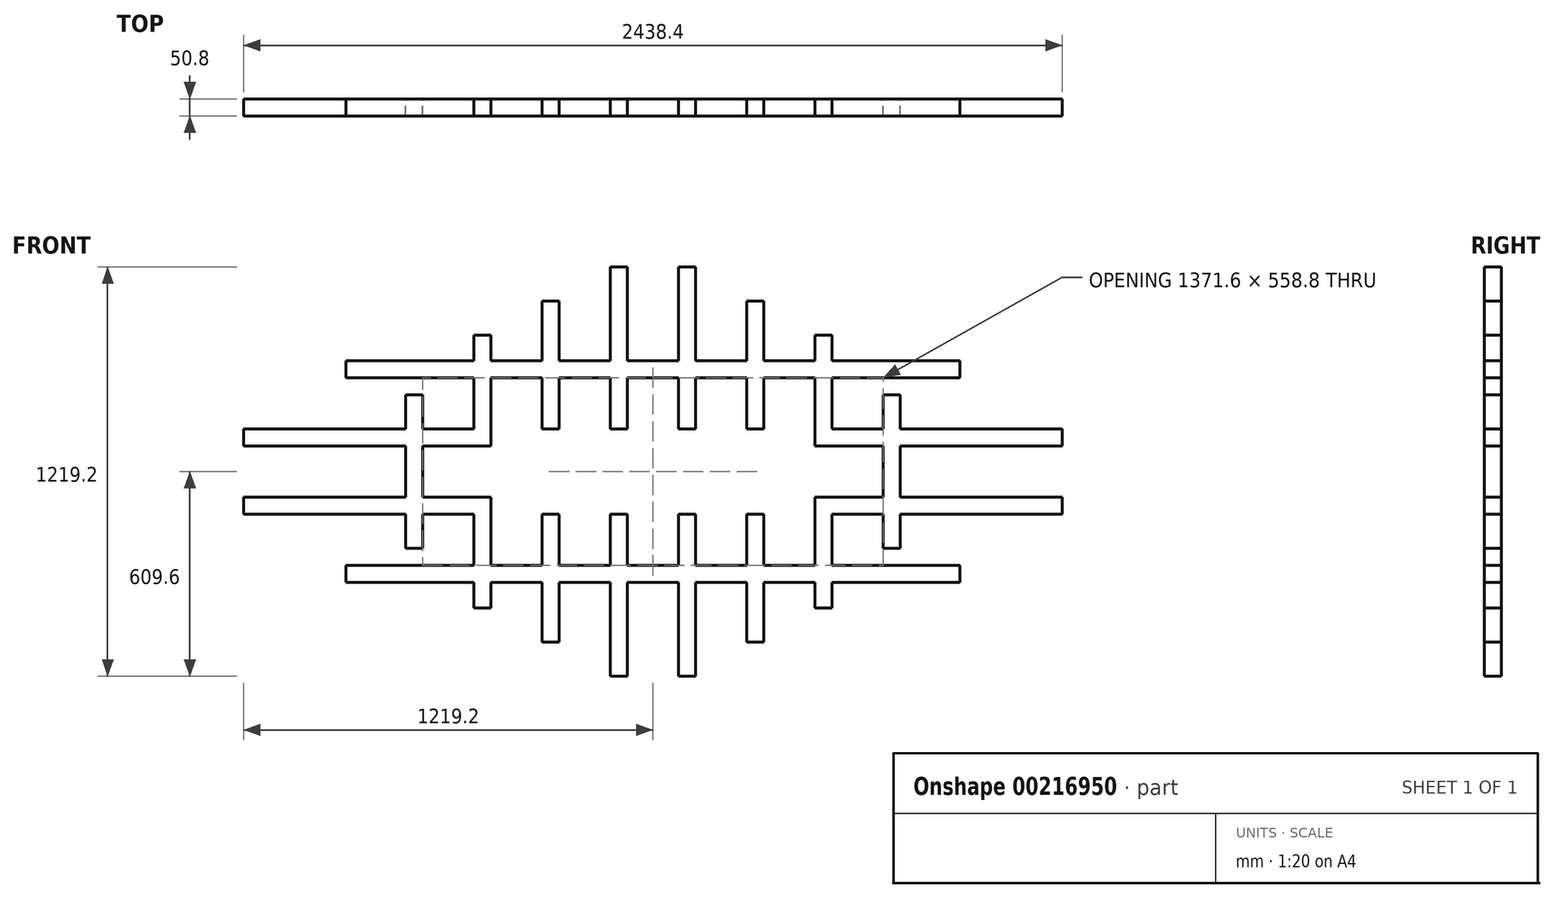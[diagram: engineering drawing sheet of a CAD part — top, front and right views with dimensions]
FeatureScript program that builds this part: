
annotation { "Feature Type Name" : "Feature", "Feature Type Description" : "" }
export const myFeature = defineFeature(function(context is Context, id is Id, definition is map)
    precondition{}
    {
        {
            var Q0;
            Q0=qCreatedBy(makeId("Front.planeOp"),FACE);
            var sketch = newSketch(context, id + "F0", { "sketchPlane" : qUnion([Q0])});
            skLineSegment(sketch, "E0.bottom", {"start": v(-1219.2, 76.2) * mm, "end": v(1219.2, 76.2) * mm});
            skLineSegment(sketch, "E0.top", {"start": v(-1219.2, -76.2) * mm, "end": v(1219.2, -76.2) * mm});
            skPoint(sketch, "E0.middle", {"position": v(0, 0) * mm});
            skLineSegment(sketch, "E1.top", {"start": v(-1219.2, 127) * mm, "end": v(1219.2, 127) * mm});
            skLineSegment(sketch, "E1.left", {"start": v(-1219.2, 76.2) * mm, "end": v(-1219.2, 127) * mm});
            skLineSegment(sketch, "E1.right", {"start": v(1219.2, 76.2) * mm, "end": v(1219.2, 127) * mm});
            skLineSegment(sketch, "E2.top", {"start": v(-1219.2, -127) * mm, "end": v(1219.2, -127) * mm});
            skLineSegment(sketch, "E2.left", {"start": v(-1219.2, -76.2) * mm, "end": v(-1219.2, -127) * mm});
            skLineSegment(sketch, "E2.right", {"start": v(1219.2, -76.2) * mm, "end": v(1219.2, -127) * mm});
            skLineSegment(sketch, "E3", {"start": v(0, -776.46) * mm, "end": v(0, 885.21) * mm, "construction": true});
            skPoint(sketch, "E3.startSnap0", {"position": v(0, -127) * mm});
            skLineSegment(sketch, "E4", {"start": v(-1506.22, 0) * mm, "end": v(1703.54, 0) * mm, "construction": true});
            skLineSegment(sketch, "E5", {"start": v(0, 127) * mm, "end": v(0, 304.8) * mm});
            skLineSegment(sketch, "E6", {"start": v(0, -127) * mm, "end": v(0, -304.8) * mm});
            skLineSegment(sketch, "E7.bottom", {"start": v(-914.4, -279.4) * mm, "end": v(914.4, -279.4) * mm});
            skLineSegment(sketch, "E7.top", {"start": v(-914.4, -330.2) * mm, "end": v(914.4, -330.2) * mm});
            skLineSegment(sketch, "E7.left", {"start": v(-914.4, -279.4) * mm, "end": v(-914.4, -330.2) * mm});
            skLineSegment(sketch, "E7.right", {"start": v(914.4, -279.4) * mm, "end": v(914.4, -330.2) * mm});
            skPoint(sketch, "E7.middle", {"position": v(0, -304.8) * mm});
            skLineSegment(sketch, "E8.bottom", {"start": v(-914.4, 330.2) * mm, "end": v(914.4, 330.2) * mm});
            skLineSegment(sketch, "E8.top", {"start": v(-914.4, 279.4) * mm, "end": v(914.4, 279.4) * mm});
            skLineSegment(sketch, "E8.left", {"start": v(-914.4, 330.2) * mm, "end": v(-914.4, 279.4) * mm});
            skLineSegment(sketch, "E8.right", {"start": v(914.4, 330.2) * mm, "end": v(914.4, 279.4) * mm});
            skPoint(sketch, "E8.middle", {"position": v(0, 304.8) * mm});
            skLineSegment(sketch, "E9", {"start": v(0, 0) * mm, "end": v(101.6, 0) * mm});
            skLineSegment(sketch, "E10", {"start": v(101.6, 0) * mm, "end": v(-101.6, 0) * mm});
            skLineSegment(sketch, "E11", {"start": v(101.6, 0) * mm, "end": v(304.8, 0) * mm});
            skLineSegment(sketch, "E12", {"start": v(304.8, 0) * mm, "end": v(508, 0) * mm});
            skLineSegment(sketch, "E13", {"start": v(508, 0) * mm, "end": v(711.2, 0) * mm});
            skLineSegment(sketch, "E14", {"start": v(-101.6, 0) * mm, "end": v(-304.8, 0) * mm});
            skLineSegment(sketch, "E15", {"start": v(-304.8, 0) * mm, "end": v(-508, 0) * mm});
            skLineSegment(sketch, "E16", {"start": v(-508, 0) * mm, "end": v(-711.2, 0) * mm});
            skLineSegment(sketch, "E17.bottom", {"start": v(127, 609.6) * mm, "end": v(76.2, 609.6) * mm});
            skLineSegment(sketch, "E17.top", {"start": v(127, -609.6) * mm, "end": v(76.2, -609.6) * mm});
            skLineSegment(sketch, "E17.left", {"start": v(127, 609.6) * mm, "end": v(127, -609.6) * mm});
            skLineSegment(sketch, "E17.right", {"start": v(76.2, 609.6) * mm, "end": v(76.2, -609.6) * mm});
            skPoint(sketch, "E17.middle", {"position": v(101.6, 0) * mm});
            skLineSegment(sketch, "E18.bottom", {"start": v(-76.2, 609.6) * mm, "end": v(-127, 609.6) * mm});
            skLineSegment(sketch, "E18.top", {"start": v(-76.2, -609.6) * mm, "end": v(-127, -609.6) * mm});
            skLineSegment(sketch, "E18.left", {"start": v(-76.2, 609.6) * mm, "end": v(-76.2, -609.6) * mm});
            skLineSegment(sketch, "E18.right", {"start": v(-127, 609.6) * mm, "end": v(-127, -609.6) * mm});
            skPoint(sketch, "E18.middle", {"position": v(-101.6, 0) * mm});
            skLineSegment(sketch, "E19.bottom", {"start": v(-278.94, 508) * mm, "end": v(-330.66, 508) * mm});
            skLineSegment(sketch, "E19.top", {"start": v(-278.94, -508) * mm, "end": v(-330.66, -508) * mm});
            skLineSegment(sketch, "E19.left", {"start": v(-278.94, 508) * mm, "end": v(-278.94, -508) * mm});
            skLineSegment(sketch, "E19.right", {"start": v(-330.66, 508) * mm, "end": v(-330.66, -508) * mm});
            skPoint(sketch, "E19.middle", {"position": v(-304.8, 0) * mm});
            skLineSegment(sketch, "E20.bottom", {"start": v(330.2, 508) * mm, "end": v(279.4, 508) * mm});
            skLineSegment(sketch, "E20.top", {"start": v(330.2, -508) * mm, "end": v(279.4, -508) * mm});
            skLineSegment(sketch, "E20.left", {"start": v(330.2, 508) * mm, "end": v(330.2, -508) * mm});
            skLineSegment(sketch, "E20.right", {"start": v(279.4, 508) * mm, "end": v(279.4, -508) * mm});
            skPoint(sketch, "E20.middle", {"position": v(304.8, 0) * mm});
            skLineSegment(sketch, "E21.bottom", {"start": v(-533.4, 406.4) * mm, "end": v(-482.6, 406.4) * mm});
            skLineSegment(sketch, "E21.top", {"start": v(-533.4, -406.4) * mm, "end": v(-482.6, -406.4) * mm});
            skLineSegment(sketch, "E21.left", {"start": v(-533.4, 406.4) * mm, "end": v(-533.4, -406.4) * mm});
            skLineSegment(sketch, "E21.right", {"start": v(-482.6, 406.4) * mm, "end": v(-482.6, -406.4) * mm});
            skPoint(sketch, "E21.middle", {"position": v(-508, 0) * mm});
            skLineSegment(sketch, "E22.bottom", {"start": v(533.4, 406.4) * mm, "end": v(482.6, 406.4) * mm});
            skLineSegment(sketch, "E22.top", {"start": v(533.4, -406.4) * mm, "end": v(482.6, -406.4) * mm});
            skLineSegment(sketch, "E22.left", {"start": v(533.4, 406.4) * mm, "end": v(533.4, -406.4) * mm});
            skLineSegment(sketch, "E22.right", {"start": v(482.6, 406.4) * mm, "end": v(482.6, -406.4) * mm});
            skPoint(sketch, "E22.middle", {"position": v(508, 0) * mm});
            skLineSegment(sketch, "E23.bottom", {"start": v(-685.8, 228.6) * mm, "end": v(-736.6, 228.6) * mm});
            skLineSegment(sketch, "E23.top", {"start": v(-685.8, -228.6) * mm, "end": v(-736.6, -228.6) * mm});
            skLineSegment(sketch, "E23.left", {"start": v(-685.8, 228.6) * mm, "end": v(-685.8, -228.6) * mm});
            skLineSegment(sketch, "E23.right", {"start": v(-736.6, 228.6) * mm, "end": v(-736.6, -228.6) * mm});
            skPoint(sketch, "E23.middle", {"position": v(-711.2, 0) * mm});
            skLineSegment(sketch, "E24.bottom", {"start": v(736.6, 228.6) * mm, "end": v(685.8, 228.6) * mm});
            skLineSegment(sketch, "E24.top", {"start": v(736.6, -228.6) * mm, "end": v(685.8, -228.6) * mm});
            skLineSegment(sketch, "E24.left", {"start": v(736.6, 228.6) * mm, "end": v(736.6, -228.6) * mm});
            skLineSegment(sketch, "E24.right", {"start": v(685.8, 228.6) * mm, "end": v(685.8, -228.6) * mm});
            skPoint(sketch, "E24.middle", {"position": v(711.2, 0) * mm});
            skSolve(sketch);
        }
        {
            var Q0;
            Q0 = qSketchRegion(id + "F0", true);
            var Q1;
            {var subQ0=sQuery(id+"F0.wireOp",EDGE,"E19.right");var subQ1=sQuery(id+"F0.wireOp",EDGE,"E1.top");var subQ2=makeQuery(id+"F0.imprint","INTERSECT",VERTEX,{"derivedFrom":[subQ1,subQ0]});Q1=makeQuery(id+"F0.imprint","IMPRINT",FACE,{"disambiguationData":[TD([[makeQuery(id+"F0.imprint","IMPRINT",EDGE,{"disambiguationData":[TD([[subQ2,-1.0]])],"derivedFrom":subQ1}),1.0]])]});}
            var Q2;
            {var subQ0=sQuery(id+"F0.wireOp",EDGE,"E18.right");var subQ1=sQuery(id+"F0.wireOp",EDGE,"E1.top");var subQ2=makeQuery(id+"F0.imprint","INTERSECT",VERTEX,{"derivedFrom":[subQ1,subQ0]});Q2=makeQuery(id+"F0.imprint","IMPRINT",FACE,{"disambiguationData":[TD([[makeQuery(id+"F0.imprint","IMPRINT",EDGE,{"disambiguationData":[TD([[subQ2,-1.0]])],"derivedFrom":subQ1}),1.0]])]});}
            var Q3;
            {var subQ0=sQuery(id+"F0.wireOp",EDGE,"E17.right");var subQ1=sQuery(id+"F0.wireOp",EDGE,"E1.top");var subQ2=makeQuery(id+"F0.imprint","INTERSECT",VERTEX,{"derivedFrom":[subQ1,subQ0]});Q3=makeQuery(id+"F0.imprint","IMPRINT",FACE,{"disambiguationData":[TD([[makeQuery(id+"F0.imprint","IMPRINT",EDGE,{"disambiguationData":[TD([[subQ2,-1.0]])],"derivedFrom":subQ1}),1.0]])]});}
            var Q4;
            {var subQ0=sQuery(id+"F0.wireOp",EDGE,"E20.right");var subQ1=sQuery(id+"F0.wireOp",EDGE,"E1.top");var subQ2=makeQuery(id+"F0.imprint","INTERSECT",VERTEX,{"derivedFrom":[subQ1,subQ0]});Q4=makeQuery(id+"F0.imprint","IMPRINT",FACE,{"disambiguationData":[TD([[makeQuery(id+"F0.imprint","IMPRINT",EDGE,{"disambiguationData":[TD([[subQ2,-1.0]])],"derivedFrom":subQ1}),1.0]])]});}
            var Q5;
            {var subQ1=sQuery(id+"F0.wireOp",EDGE,"E0.bottom");var subQ7=sQuery(id+"F0.wireOp",EDGE,"E20.right");var subQ8=makeQuery(id+"F0.imprint","INTERSECT",VERTEX,{"derivedFrom":[subQ1,subQ7]});Q5=makeQuery(id+"F0.imprint","IMPRINT",FACE,{"disambiguationData":[TD([[makeQuery(id+"F0.imprint","IMPRINT",EDGE,{"disambiguationData":[TD([[subQ8,-1.0]])],"derivedFrom":subQ1}),-1.0]])]});}
            var Q6;
            {var subQ1=sQuery(id+"F0.wireOp",EDGE,"E0.top");var subQ7=sQuery(id+"F0.wireOp",EDGE,"E20.right");var subQ9=makeQuery(id+"F0.imprint","INTERSECT",VERTEX,{"derivedFrom":[subQ1,subQ7]});Q6=makeQuery(id+"F0.imprint","IMPRINT",FACE,{"disambiguationData":[TD([[makeQuery(id+"F0.imprint","IMPRINT",EDGE,{"disambiguationData":[TD([[subQ9,-1.0]])],"derivedFrom":subQ1}),1.0]])]});}
            var Q7;
            {var subQ0=sQuery(id+"F0.wireOp",EDGE,"E20.right");var subQ1=sQuery(id+"F0.wireOp",EDGE,"E0.top");var subQ2=makeQuery(id+"F0.imprint","INTERSECT",VERTEX,{"derivedFrom":[subQ1,subQ0]});Q7=makeQuery(id+"F0.imprint","IMPRINT",FACE,{"disambiguationData":[TD([[makeQuery(id+"F0.imprint","IMPRINT",EDGE,{"disambiguationData":[TD([[subQ2,-1.0]])],"derivedFrom":subQ1}),-1.0]])]});}
            var Q8;
            {var subQ0=sQuery(id+"F0.wireOp",EDGE,"E20.right");var subQ1=sQuery(id+"F0.wireOp",EDGE,"E2.top");var subQ2=makeQuery(id+"F0.imprint","INTERSECT",VERTEX,{"derivedFrom":[subQ1,subQ0]});Q8=makeQuery(id+"F0.imprint","IMPRINT",FACE,{"disambiguationData":[TD([[makeQuery(id+"F0.imprint","IMPRINT",EDGE,{"disambiguationData":[TD([[subQ2,-1.0]])],"derivedFrom":subQ1}),-1.0]])]});}
            var Q9;
            {var subQ0=sQuery(id+"F0.wireOp",EDGE,"E20.right");var subQ1=sQuery(id+"F0.wireOp",EDGE,"E0.bottom");var subQ2=makeQuery(id+"F0.imprint","INTERSECT",VERTEX,{"derivedFrom":[subQ1,subQ0]});Q9=makeQuery(id+"F0.imprint","IMPRINT",FACE,{"disambiguationData":[TD([[makeQuery(id+"F0.imprint","IMPRINT",EDGE,{"disambiguationData":[TD([[subQ2,-1.0]])],"derivedFrom":subQ1}),1.0]])]});}
            var Q10;
            {var subQ5=sQuery(id+"F0.wireOp",EDGE,"E0.bottom");var subQ7=sQuery(id+"F0.wireOp",EDGE,"E22.right");var subQ9=makeQuery(id+"F0.imprint","INTERSECT",VERTEX,{"derivedFrom":[subQ5,subQ7]});Q10=makeQuery(id+"F0.imprint","IMPRINT",FACE,{"disambiguationData":[TD([[makeQuery(id+"F0.imprint","IMPRINT",EDGE,{"disambiguationData":[TD([[subQ9,-1.0]])],"derivedFrom":subQ5}),-1.0]])]});}
            var Q11;
            {var subQ5=sQuery(id+"F0.wireOp",EDGE,"E0.top");var subQ7=sQuery(id+"F0.wireOp",EDGE,"E22.right");var subQ8=makeQuery(id+"F0.imprint","INTERSECT",VERTEX,{"derivedFrom":[subQ5,subQ7]});Q11=makeQuery(id+"F0.imprint","IMPRINT",FACE,{"disambiguationData":[TD([[makeQuery(id+"F0.imprint","IMPRINT",EDGE,{"disambiguationData":[TD([[subQ8,-1.0]])],"derivedFrom":subQ5}),1.0]])]});}
            var Q12;
            {var subQ0=sQuery(id+"F0.wireOp",EDGE,"E17.right");var subQ1=sQuery(id+"F0.wireOp",EDGE,"E2.top");var subQ2=makeQuery(id+"F0.imprint","INTERSECT",VERTEX,{"derivedFrom":[subQ1,subQ0]});Q12=makeQuery(id+"F0.imprint","IMPRINT",FACE,{"disambiguationData":[TD([[makeQuery(id+"F0.imprint","IMPRINT",EDGE,{"disambiguationData":[TD([[subQ2,-1.0]])],"derivedFrom":subQ1}),-1.0]])]});}
            var Q13;
            {var subQ0=sQuery(id+"F0.wireOp",EDGE,"E17.right");var subQ1=sQuery(id+"F0.wireOp",EDGE,"E0.top");var subQ2=makeQuery(id+"F0.imprint","INTERSECT",VERTEX,{"derivedFrom":[subQ1,subQ0]});Q13=makeQuery(id+"F0.imprint","IMPRINT",FACE,{"disambiguationData":[TD([[makeQuery(id+"F0.imprint","IMPRINT",EDGE,{"disambiguationData":[TD([[subQ2,-1.0]])],"derivedFrom":subQ1}),-1.0]])]});}
            var Q14;
            {var subQ1=sQuery(id+"F0.wireOp",EDGE,"E0.top");var subQ7=sQuery(id+"F0.wireOp",EDGE,"E17.right");var subQ9=makeQuery(id+"F0.imprint","INTERSECT",VERTEX,{"derivedFrom":[subQ1,subQ7]});Q14=makeQuery(id+"F0.imprint","IMPRINT",FACE,{"disambiguationData":[TD([[makeQuery(id+"F0.imprint","IMPRINT",EDGE,{"disambiguationData":[TD([[subQ9,-1.0]])],"derivedFrom":subQ1}),1.0]])]});}
            var Q15;
            {var subQ1=sQuery(id+"F0.wireOp",EDGE,"E0.bottom");var subQ7=sQuery(id+"F0.wireOp",EDGE,"E17.right");var subQ9=makeQuery(id+"F0.imprint","INTERSECT",VERTEX,{"derivedFrom":[subQ1,subQ7]});Q15=makeQuery(id+"F0.imprint","IMPRINT",FACE,{"disambiguationData":[TD([[makeQuery(id+"F0.imprint","IMPRINT",EDGE,{"disambiguationData":[TD([[subQ9,-1.0]])],"derivedFrom":subQ1}),-1.0]])]});}
            var Q16;
            {var subQ0=sQuery(id+"F0.wireOp",EDGE,"E17.right");var subQ1=sQuery(id+"F0.wireOp",EDGE,"E0.bottom");var subQ2=makeQuery(id+"F0.imprint","INTERSECT",VERTEX,{"derivedFrom":[subQ1,subQ0]});Q16=makeQuery(id+"F0.imprint","IMPRINT",FACE,{"disambiguationData":[TD([[makeQuery(id+"F0.imprint","IMPRINT",EDGE,{"disambiguationData":[TD([[subQ2,-1.0]])],"derivedFrom":subQ1}),1.0]])]});}
            var Q17;
            {var subQ0=sQuery(id+"F0.wireOp",EDGE,"E18.right");var subQ1=sQuery(id+"F0.wireOp",EDGE,"E0.bottom");var subQ2=makeQuery(id+"F0.imprint","INTERSECT",VERTEX,{"derivedFrom":[subQ1,subQ0]});Q17=makeQuery(id+"F0.imprint","IMPRINT",FACE,{"disambiguationData":[TD([[makeQuery(id+"F0.imprint","IMPRINT",EDGE,{"disambiguationData":[TD([[subQ2,-1.0]])],"derivedFrom":subQ1}),1.0]])]});}
            var Q18;
            {var subQ1=sQuery(id+"F0.wireOp",EDGE,"E0.bottom");var subQ7=sQuery(id+"F0.wireOp",EDGE,"E18.right");var subQ9=makeQuery(id+"F0.imprint","INTERSECT",VERTEX,{"derivedFrom":[subQ1,subQ7]});Q18=makeQuery(id+"F0.imprint","IMPRINT",FACE,{"disambiguationData":[TD([[makeQuery(id+"F0.imprint","IMPRINT",EDGE,{"disambiguationData":[TD([[subQ9,-1.0]])],"derivedFrom":subQ1}),-1.0]])]});}
            var Q19;
            {var subQ3=sQuery(id+"F0.wireOp",EDGE,"E18.right");var subQ7=sQuery(id+"F0.wireOp",EDGE,"E0.top");var subQ9=makeQuery(id+"F0.imprint","INTERSECT",VERTEX,{"derivedFrom":[subQ7,subQ3]});Q19=makeQuery(id+"F0.imprint","IMPRINT",FACE,{"disambiguationData":[TD([[makeQuery(id+"F0.imprint","IMPRINT",EDGE,{"disambiguationData":[TD([[subQ9,-1.0]])],"derivedFrom":subQ7}),1.0]])]});}
            var Q20;
            {var subQ0=sQuery(id+"F0.wireOp",EDGE,"E18.right");var subQ1=sQuery(id+"F0.wireOp",EDGE,"E0.top");var subQ2=makeQuery(id+"F0.imprint","INTERSECT",VERTEX,{"derivedFrom":[subQ1,subQ0]});Q20=makeQuery(id+"F0.imprint","IMPRINT",FACE,{"disambiguationData":[TD([[makeQuery(id+"F0.imprint","IMPRINT",EDGE,{"disambiguationData":[TD([[subQ2,-1.0]])],"derivedFrom":subQ1}),-1.0]])]});}
            var Q21;
            {var subQ0=sQuery(id+"F0.wireOp",EDGE,"E18.right");var subQ1=sQuery(id+"F0.wireOp",EDGE,"E2.top");var subQ2=makeQuery(id+"F0.imprint","INTERSECT",VERTEX,{"derivedFrom":[subQ1,subQ0]});Q21=makeQuery(id+"F0.imprint","IMPRINT",FACE,{"disambiguationData":[TD([[makeQuery(id+"F0.imprint","IMPRINT",EDGE,{"disambiguationData":[TD([[subQ2,-1.0]])],"derivedFrom":subQ1}),-1.0]])]});}
            var Q22;
            {var subQ0=sQuery(id+"F0.wireOp",EDGE,"E19.right");var subQ1=sQuery(id+"F0.wireOp",EDGE,"E2.top");var subQ2=makeQuery(id+"F0.imprint","INTERSECT",VERTEX,{"derivedFrom":[subQ1,subQ0]});Q22=makeQuery(id+"F0.imprint","IMPRINT",FACE,{"disambiguationData":[TD([[makeQuery(id+"F0.imprint","IMPRINT",EDGE,{"disambiguationData":[TD([[subQ2,-1.0]])],"derivedFrom":subQ1}),-1.0]])]});}
            var Q23;
            {var subQ0=sQuery(id+"F0.wireOp",EDGE,"E19.right");var subQ1=sQuery(id+"F0.wireOp",EDGE,"E0.top");var subQ2=makeQuery(id+"F0.imprint","INTERSECT",VERTEX,{"derivedFrom":[subQ1,subQ0]});Q23=makeQuery(id+"F0.imprint","IMPRINT",FACE,{"disambiguationData":[TD([[makeQuery(id+"F0.imprint","IMPRINT",EDGE,{"disambiguationData":[TD([[subQ2,-1.0]])],"derivedFrom":subQ1}),-1.0]])]});}
            var Q24;
            {var subQ1=sQuery(id+"F0.wireOp",EDGE,"E0.top");var subQ7=sQuery(id+"F0.wireOp",EDGE,"E19.right");var subQ9=makeQuery(id+"F0.imprint","INTERSECT",VERTEX,{"derivedFrom":[subQ1,subQ7]});Q24=makeQuery(id+"F0.imprint","IMPRINT",FACE,{"disambiguationData":[TD([[makeQuery(id+"F0.imprint","IMPRINT",EDGE,{"disambiguationData":[TD([[subQ9,-1.0]])],"derivedFrom":subQ1}),1.0]])]});}
            var Q25;
            {var subQ1=sQuery(id+"F0.wireOp",EDGE,"E0.bottom");var subQ7=sQuery(id+"F0.wireOp",EDGE,"E19.right");var subQ9=makeQuery(id+"F0.imprint","INTERSECT",VERTEX,{"derivedFrom":[subQ1,subQ7]});Q25=makeQuery(id+"F0.imprint","IMPRINT",FACE,{"disambiguationData":[TD([[makeQuery(id+"F0.imprint","IMPRINT",EDGE,{"disambiguationData":[TD([[subQ9,-1.0]])],"derivedFrom":subQ1}),-1.0]])]});}
            var Q26;
            {var subQ0=sQuery(id+"F0.wireOp",EDGE,"E19.right");var subQ1=sQuery(id+"F0.wireOp",EDGE,"E0.bottom");var subQ2=makeQuery(id+"F0.imprint","INTERSECT",VERTEX,{"derivedFrom":[subQ1,subQ0]});Q26=makeQuery(id+"F0.imprint","IMPRINT",FACE,{"disambiguationData":[TD([[makeQuery(id+"F0.imprint","IMPRINT",EDGE,{"disambiguationData":[TD([[subQ2,-1.0]])],"derivedFrom":subQ1}),1.0]])]});}
            var Q27;
            {var subQ0=sQuery(id+"F0.wireOp",EDGE,"E21.left");var subQ1=sQuery(id+"F0.wireOp",EDGE,"E0.bottom");var subQ2=makeQuery(id+"F0.imprint","INTERSECT",VERTEX,{"derivedFrom":[subQ1,subQ0]});Q27=makeQuery(id+"F0.imprint","IMPRINT",FACE,{"disambiguationData":[TD([[makeQuery(id+"F0.imprint","IMPRINT",EDGE,{"disambiguationData":[TD([[subQ2,-1.0]])],"derivedFrom":subQ1}),-1.0]])]});}
            var Q28;
            {var subQ0=sQuery(id+"F0.wireOp",EDGE,"E21.left");var subQ1=sQuery(id+"F0.wireOp",EDGE,"E0.top");var subQ2=makeQuery(id+"F0.imprint","INTERSECT",VERTEX,{"derivedFrom":[subQ1,subQ0]});Q28=makeQuery(id+"F0.imprint","IMPRINT",FACE,{"disambiguationData":[TD([[makeQuery(id+"F0.imprint","IMPRINT",EDGE,{"disambiguationData":[TD([[subQ2,-1.0]])],"derivedFrom":subQ1}),1.0]])]});}
            var Q29;
            {var subQ0=sQuery(id+"F0.wireOp",EDGE,"E21.right");var subQ1=sQuery(id+"F0.wireOp",EDGE,"E0.bottom");var subQ2=makeQuery(id+"F0.imprint","INTERSECT",VERTEX,{"derivedFrom":[subQ1,subQ0]});Q29=makeQuery(id+"F0.imprint","IMPRINT",FACE,{"disambiguationData":[TD([[makeQuery(id+"F0.imprint","IMPRINT",EDGE,{"disambiguationData":[TD([[subQ2,-1.0]])],"derivedFrom":subQ1}),1.0]])]});}
            var Q30;
            {var subQ0=sQuery(id+"F0.wireOp",EDGE,"E19.left");var subQ1=sQuery(id+"F0.wireOp",EDGE,"E0.bottom");var subQ2=makeQuery(id+"F0.imprint","INTERSECT",VERTEX,{"derivedFrom":[subQ1,subQ0]});Q30=makeQuery(id+"F0.imprint","IMPRINT",FACE,{"disambiguationData":[TD([[makeQuery(id+"F0.imprint","IMPRINT",EDGE,{"disambiguationData":[TD([[subQ2,-1.0]])],"derivedFrom":subQ1}),1.0]])]});}
            var Q31;
            {var subQ1=sQuery(id+"F0.wireOp",EDGE,"E0.bottom");var subQ6=sQuery(id+"F0.wireOp",EDGE,"E18.left");var subQ7=makeQuery(id+"F0.imprint","INTERSECT",VERTEX,{"derivedFrom":[subQ1,subQ6]});Q31=makeQuery(id+"F0.imprint","IMPRINT",FACE,{"disambiguationData":[TD([[makeQuery(id+"F0.imprint","IMPRINT",EDGE,{"disambiguationData":[TD([[subQ7,-1.0]])],"derivedFrom":subQ1}),1.0]])]});}
            var Q32;
            {var subQ0=sQuery(id+"F0.wireOp",EDGE,"E17.left");var subQ1=sQuery(id+"F0.wireOp",EDGE,"E0.bottom");var subQ2=makeQuery(id+"F0.imprint","INTERSECT",VERTEX,{"derivedFrom":[subQ1,subQ0]});Q32=makeQuery(id+"F0.imprint","IMPRINT",FACE,{"disambiguationData":[TD([[makeQuery(id+"F0.imprint","IMPRINT",EDGE,{"disambiguationData":[TD([[subQ2,-1.0]])],"derivedFrom":subQ1}),1.0]])]});}
            var Q33;
            {var subQ0=sQuery(id+"F0.wireOp",EDGE,"E20.left");var subQ1=sQuery(id+"F0.wireOp",EDGE,"E0.bottom");var subQ2=makeQuery(id+"F0.imprint","INTERSECT",VERTEX,{"derivedFrom":[subQ1,subQ0]});Q33=makeQuery(id+"F0.imprint","IMPRINT",FACE,{"disambiguationData":[TD([[makeQuery(id+"F0.imprint","IMPRINT",EDGE,{"disambiguationData":[TD([[subQ2,-1.0]])],"derivedFrom":subQ1}),1.0]])]});}
            var Q34;
            {var subQ0=sQuery(id+"F0.wireOp",EDGE,"E20.left");var subQ1=sQuery(id+"F0.wireOp",EDGE,"E0.top");var subQ2=makeQuery(id+"F0.imprint","INTERSECT",VERTEX,{"derivedFrom":[subQ1,subQ0]});Q34=makeQuery(id+"F0.imprint","IMPRINT",FACE,{"disambiguationData":[TD([[makeQuery(id+"F0.imprint","IMPRINT",EDGE,{"disambiguationData":[TD([[subQ2,-1.0]])],"derivedFrom":subQ1}),-1.0]])]});}
            var Q35;
            {var subQ0=sQuery(id+"F0.wireOp",EDGE,"E17.left");var subQ1=sQuery(id+"F0.wireOp",EDGE,"E0.top");var subQ2=makeQuery(id+"F0.imprint","INTERSECT",VERTEX,{"derivedFrom":[subQ1,subQ0]});Q35=makeQuery(id+"F0.imprint","IMPRINT",FACE,{"disambiguationData":[TD([[makeQuery(id+"F0.imprint","IMPRINT",EDGE,{"disambiguationData":[TD([[subQ2,-1.0]])],"derivedFrom":subQ1}),-1.0]])]});}
            var Q36;
            {var subQ1=sQuery(id+"F0.wireOp",EDGE,"E0.top");var subQ6=sQuery(id+"F0.wireOp",EDGE,"E18.left");var subQ7=makeQuery(id+"F0.imprint","INTERSECT",VERTEX,{"derivedFrom":[subQ1,subQ6]});Q36=makeQuery(id+"F0.imprint","IMPRINT",FACE,{"disambiguationData":[TD([[makeQuery(id+"F0.imprint","IMPRINT",EDGE,{"disambiguationData":[TD([[subQ7,-1.0]])],"derivedFrom":subQ1}),-1.0]])]});}
            var Q37;
            {var subQ0=sQuery(id+"F0.wireOp",EDGE,"E19.left");var subQ1=sQuery(id+"F0.wireOp",EDGE,"E0.top");var subQ2=makeQuery(id+"F0.imprint","INTERSECT",VERTEX,{"derivedFrom":[subQ1,subQ0]});Q37=makeQuery(id+"F0.imprint","IMPRINT",FACE,{"disambiguationData":[TD([[makeQuery(id+"F0.imprint","IMPRINT",EDGE,{"disambiguationData":[TD([[subQ2,-1.0]])],"derivedFrom":subQ1}),-1.0]])]});}
            var Q38;
            {var subQ0=sQuery(id+"F0.wireOp",EDGE,"E21.right");var subQ1=sQuery(id+"F0.wireOp",EDGE,"E0.top");var subQ2=makeQuery(id+"F0.imprint","INTERSECT",VERTEX,{"derivedFrom":[subQ1,subQ0]});Q38=makeQuery(id+"F0.imprint","IMPRINT",FACE,{"disambiguationData":[TD([[makeQuery(id+"F0.imprint","IMPRINT",EDGE,{"disambiguationData":[TD([[subQ2,-1.0]])],"derivedFrom":subQ1}),-1.0]])]});}
            extrude(context, id + "F1", {"entities" : qUnion([Q0, Q1, Q2, Q3, Q4, Q5, Q6, Q7, Q8, Q9, Q10, Q11, Q12, Q13, Q14, Q15, Q16, Q17, Q18, Q19, Q20, Q21, Q22, Q23, Q24, Q25, Q26, Q27, Q28, Q29, Q30, Q31, Q32, Q33, Q34, Q35, Q36, Q37, Q38]), "depth" : 50.8 * mm});
        }
    });
